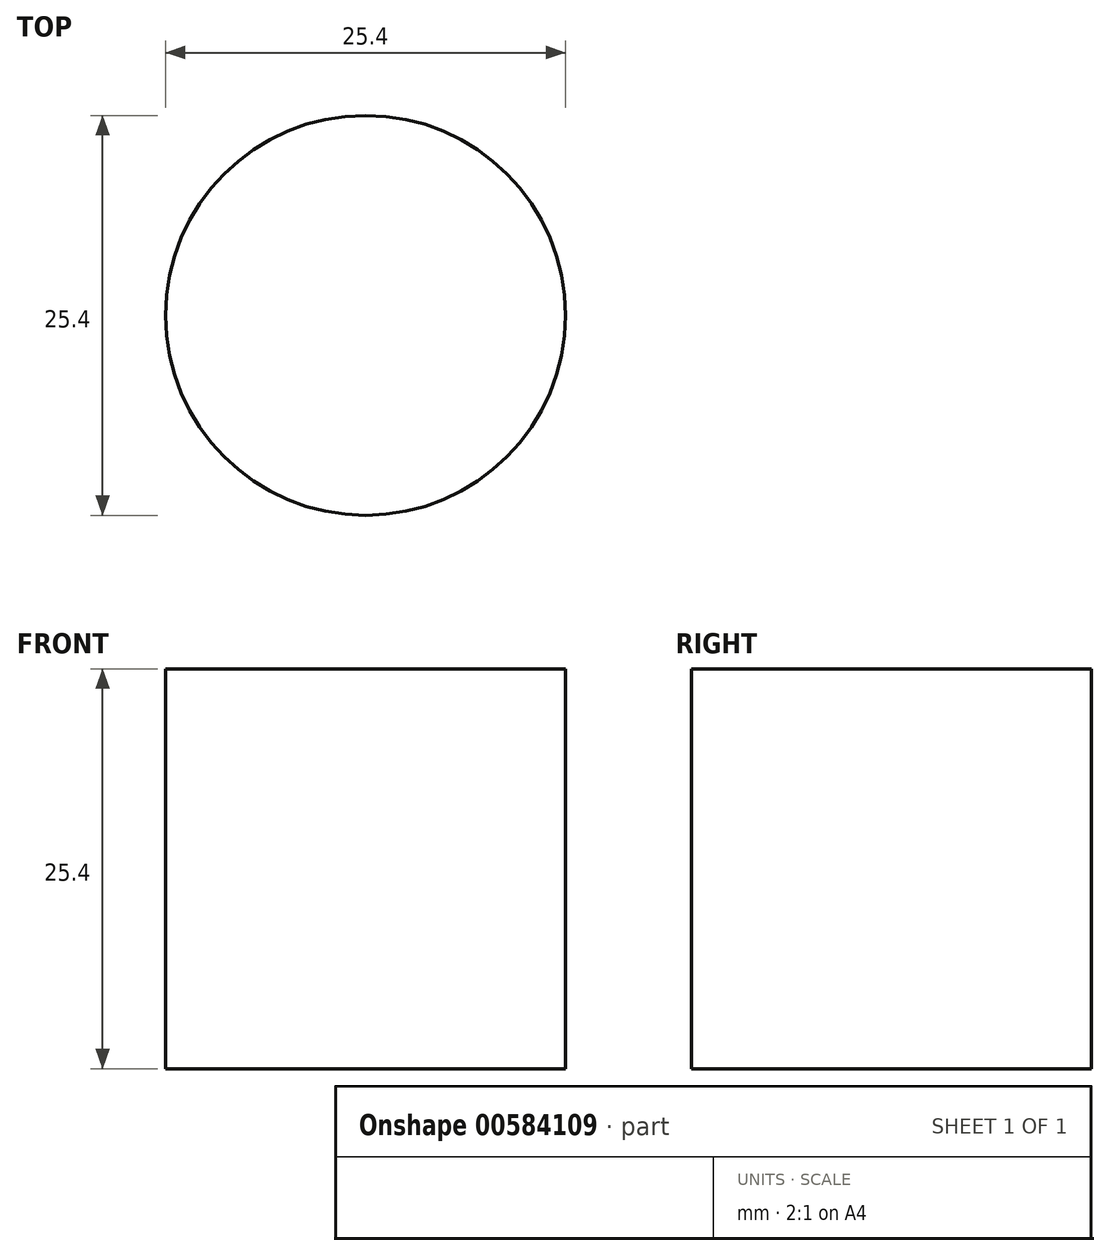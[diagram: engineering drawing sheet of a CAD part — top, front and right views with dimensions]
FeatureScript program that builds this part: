
annotation { "Feature Type Name" : "Feature", "Feature Type Description" : "" }
export const myFeature = defineFeature(function(context is Context, id is Id, definition is map)
    precondition{}
    {
        {
            var Q0;
            Q0=qCreatedBy(makeId("Top.planeOp"),FACE);
            var sketch = newSketch(context, id + "F0", { "sketchPlane" : qUnion([Q0])});
            skCircle(sketch, "E0", {"center": v(0, 0) * mm, "radius": 12.7 * mm});
            skSolve(sketch);
        }
        {
            var Q0;
            Q0=makeQuery(id+"F0.imprint","IMPRINT",FACE,{"disambiguationData":[TD([[makeQuery(id+"F0.imprint","IMPRINT",EDGE,{"derivedFrom":sQuery(id+"F0.wireOp",EDGE,"E0")}),1.0]])]});
            extrude(context, id + "F1", {"entities" : qUnion([Q0]), "depth" : 25.4 * mm, "offsetDistance" : 25.4 * mm});
        }
        {
            var Q0;
            Q0=qCreatedBy(makeId("Front.planeOp"),FACE);
            var sketch = newSketch(context, id + "F2", { "sketchPlane" : qUnion([Q0])});
            skCircle(sketch, "E1", {"center": v(0, 12.7) * mm, "radius": 12.7 * mm});
            skSolve(sketch);
        }
        {
            var Q0;
            Q0=sQuery(id+"F2.wireOp",EDGE,"E1");
            extrude(context, id + "F3", {"bodyType" : ToolBodyType.SURFACE, "surfaceEntities" : qUnion([Q0]), "oppositeDirection" : true, "depth" : 25.4 * mm, "offsetDistance" : 25.4 * mm});
        }
    });
